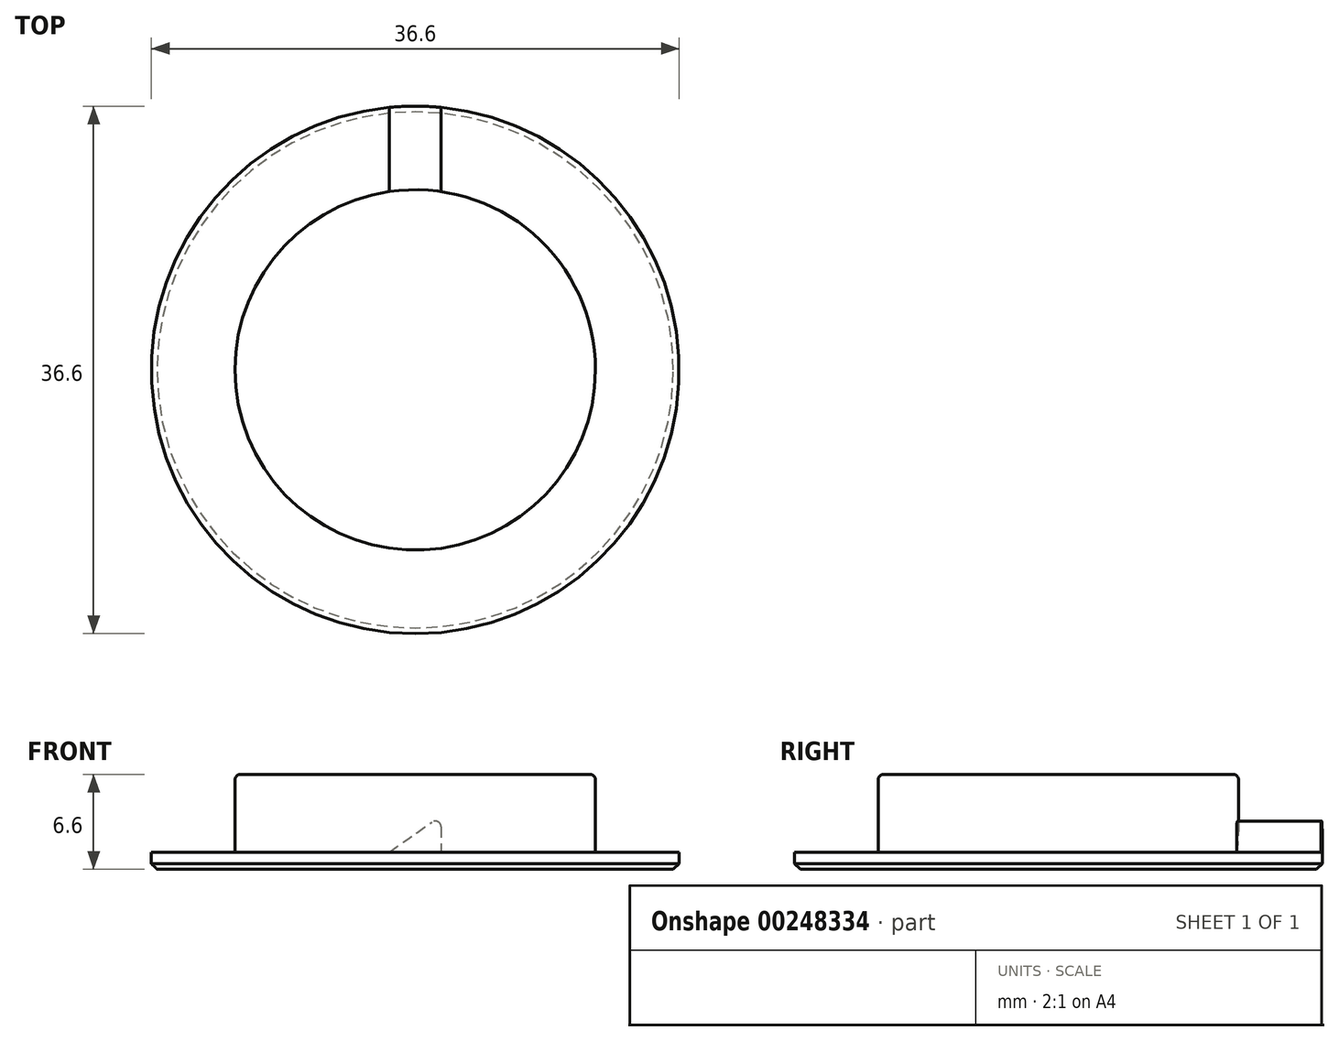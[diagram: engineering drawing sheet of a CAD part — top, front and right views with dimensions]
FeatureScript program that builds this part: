
annotation { "Feature Type Name" : "Feature", "Feature Type Description" : "" }
export const myFeature = defineFeature(function(context is Context, id is Id, definition is map)
    precondition{}
    {
        {
            var Q0;
            Q0=qCreatedBy(makeId("Top.planeOp"),FACE);
            var sketch = newSketch(context, id + "F0", { "sketchPlane" : qUnion([Q0])});
            skCircle(sketch, "E0", {"center": v(0, 0) * mm, "radius": 12.5 * mm});
            skSolve(sketch);
        }
        {
            var Q0;
            Q0 = qSketchRegion(id + "F0", true);
            extrude(context, id + "F1", {"entities" : qUnion([Q0]), "depth" : 5.4 * mm});
        }
        {
            var Q0;
            Q0=makeQuery(id+"F1.opExtrude","CAP_FACE",FACE,{"disambiguationData":[OSD([sQuery(id+"F0.wireOp",EDGE,"E0")])],"isStart":true});
            var sketch = newSketch(context, id + "F2", { "sketchPlane" : qUnion([Q0])});
            skCircle(sketch, "E1", {"center": v(0, 0) * mm, "radius": 18.3 * mm});
            skSolve(sketch);
        }
        {
            var Q0;
            Q0 = qSketchRegion(id + "F2", true);
            extrude(context, id + "F3", {"entities" : qUnion([Q0]), "operationType" : NewBodyOperationType.ADD, "depth" : 1.2 * mm});
        }
        {
            var Q0;
            Q0=qCreatedBy(makeId("Front.planeOp"),FACE);
            var sketch = newSketch(context, id + "F4", { "sketchPlane" : qUnion([Q0])});
            skLineSegment(sketch, "E2", {"start": v(0, 0) * mm, "end": v(0, 1.26) * mm, "construction": true});
            skLineSegment(sketch, "E3", {"start": v(0, 1.26) * mm, "end": v(1.8, 2.52) * mm});
            skLineSegment(sketch, "E4", {"start": v(1.8, 2.52) * mm, "end": v(-1.8, 2.52) * mm, "construction": true});
            skLineSegment(sketch, "E5", {"start": v(-1.8, 2.52) * mm, "end": v(-1.8, 0) * mm, "construction": true});
            skLineSegment(sketch, "E6", {"start": v(0, 1.26) * mm, "end": v(-1.8, 0) * mm});
            skLineSegment(sketch, "E7", {"start": v(1.8, 2.52) * mm, "end": v(1.8, 0) * mm});
            skLineSegment(sketch, "E8", {"start": v(1.8, 0) * mm, "end": v(-1.8, 0) * mm});
            skSolve(sketch);
        }
        {
            var Q0;
            Q0 = qSketchRegion(id + "F4", true);
            var Q1;
            Q1=makeQuery(id+"F3.opExtrude","SWEPT_FACE",FACE,{"disambiguationData":[OSD([sQuery(id+"F2.wireOp",EDGE,"E1")])]});
            extrude(context, id + "F5", {"entities" : qUnion([Q0]), "operationType" : NewBodyOperationType.ADD, "endBound" : BoundingType.UP_TO_SURFACE, "oppositeDirection" : true, "endBoundEntityFace" : qUnion([Q1]), "depth" : 25 * mm});
        }
        {
            var Q0;
            Q0=makeQuery(id+"F5.opExtrude","SWEPT_EDGE",EDGE,{"disambiguationData":[OSD([sQuery(id+"F4.wireOp",EDGE,"E3"),sQuery(id+"F4.wireOp",EDGE,"E7")])]});
            fillet(context, id + "F6", {"entities" : qUnion([Q0]), "radius" : 0.4 * mm, "tangentPropagation" : true, "allowEdgeOverflow" : false});
        }
        {
            var Q0;
            Q0=makeQuery(id+"F1.opExtrude","CAP_EDGE",EDGE,{"disambiguationData":[OSD([sQuery(id+"F0.wireOp",EDGE,"E0")])],"isStart":false});
            fillet(context, id + "F7", {"entities" : qUnion([Q0]), "radius" : 0.4 * mm, "tangentPropagation" : true, "allowEdgeOverflow" : false});
        }
        {
            var Q0;
            Q0=makeQuery(id+"F3.opExtrude","CAP_EDGE",EDGE,{"disambiguationData":[OSD([sQuery(id+"F2.wireOp",EDGE,"E1")])],"isStart":false});
            chamfer(context, id + "F8", {"entities" : qUnion([Q0]), "width" : 0.4 * mm, "tangentPropagation" : true});
        }
    });
